# Revit family: 33_O13111001_Taza Baltico Entrada Superior
name_source: partatom
category: Aparatos sanitarios
revit_build: Autodesk Revit 2018 (Build: 20170223_1515(x64)
units: mm (PartAtom-declared; Revit-internal decimal feet)

## family parameters
Anfitrión = Cara
Compartido = No
Corte con vacíos al cargar = No
Cota de conector redondo = Diámetro de uso
Número OmniClass = 23.45.05.21.11.11
Punto de cálculo de habitación = No
Tipo de pieza = Normal
Título OmniClass = Water Operated Water Closets

## types (1)
- 33_O13111001_Taza Baltico Entrada Superior
    Capacidad de descarga = 1000 gr
    Consumo de Agua = 4.8 Lt por descarga
    Cumple EDGE = Si
    Cumple LEED = Si
    Elevación por defecto = 1219 mm
    Garantia = Garantía CORONA limitada de por vida en elementos de porcelana y 5 años en grifería tanque y asiento
    Marca = CORONA
    Material = Cerámica
    Nombre = Taza Baltico Entrada Superior
    Presión Máxima = 80 PSI
    Presión Mínima = 35 PSI
    Referencia = O13111001
    Tipo = Taza
    URL = https://www.corona.co
